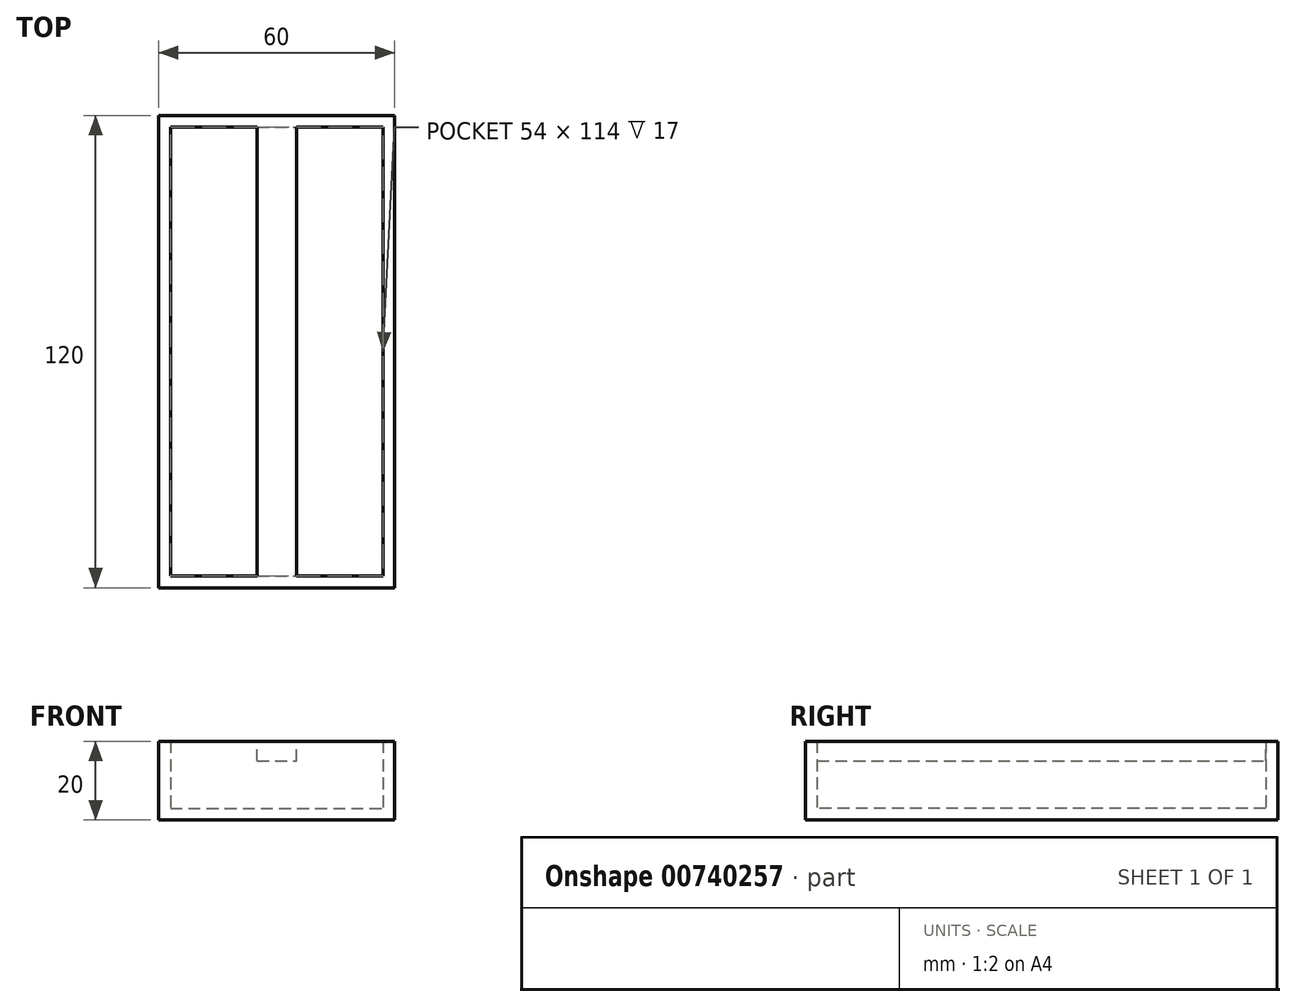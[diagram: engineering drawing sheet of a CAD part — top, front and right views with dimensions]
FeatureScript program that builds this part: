
annotation { "Feature Type Name" : "Feature", "Feature Type Description" : "" }
export const myFeature = defineFeature(function(context is Context, id is Id, definition is map)
    precondition{}
    {
        {
            var Q0;
            Q0=qCreatedBy(makeId("Top.planeOp"),FACE);
            var sketch = newSketch(context, id + "F0", { "sketchPlane" : qUnion([Q0])});
            skLineSegment(sketch, "E0.bottom", {"start": v(-30, 60) * mm, "end": v(30, 60) * mm});
            skLineSegment(sketch, "E0.top", {"start": v(-30, -60) * mm, "end": v(30, -60) * mm});
            skLineSegment(sketch, "E0.left", {"start": v(-30, 60) * mm, "end": v(-30, -60) * mm});
            skLineSegment(sketch, "E0.right", {"start": v(30, 60) * mm, "end": v(30, -60) * mm});
            skPoint(sketch, "E0.middle", {"position": v(0, 0) * mm});
            skSolve(sketch);
        }
        {
            var Q0;
            Q0 = qSketchRegion(id + "F0", true);
            extrude(context, id + "F1", {"entities" : qUnion([Q0]), "depth" : 20 * mm, "offsetDistance" : 25 * mm});
        }
        {
            var Q0;
            Q0=makeQuery(id+"F1.opExtrude","CAP_FACE",FACE,{"disambiguationData":[OSD([sQuery(id+"F0.wireOp",EDGE,"E0.bottom"),sQuery(id+"F0.wireOp",EDGE,"E0.top"),sQuery(id+"F0.wireOp",EDGE,"E0.left"),sQuery(id+"F0.wireOp",EDGE,"E0.right")])],"isStart":false});
            shell(context, id + "F2", {"entities" : qUnion([Q0]), "thickness" : 3 * mm});
        }
        {
            var Q0;
            Q0=qCreatedBy(makeId("Front.planeOp"),FACE);
            var sketch = newSketch(context, id + "F3", { "sketchPlane" : qUnion([Q0])});
            skLineSegment(sketch, "E1.bottom", {"start": v(5, 20) * mm, "end": v(-5, 20) * mm});
            skLineSegment(sketch, "E1.left", {"start": v(5, 20) * mm, "end": v(5, 15) * mm});
            skLineSegment(sketch, "E1.right", {"start": v(-5, 20) * mm, "end": v(-5, 15) * mm});
            skPoint(sketch, "E1.middle", {"position": v(0, 0) * mm});
            skLineSegment(sketch, "E2", {"start": v(5, 15) * mm, "end": v(-5, 15) * mm});
            skPoint(sketch, "E1.top.end.orphan", {"position": v(-5, -20) * mm});
            skPoint(sketch, "E1.top.start.orphan", {"position": v(5, -20) * mm});
            skSolve(sketch);
        }
        {
            var Q0;
            Q0 = qSketchRegion(id + "F3", true);
            extrude(context, id + "F4", {"entities" : qUnion([Q0]), "operationType" : NewBodyOperationType.ADD, "depth" : 60 * mm, "offsetDistance" : 25 * mm});
        }
        {
            var Q0;
            Q0 = qSketchRegion(id + "F3", true);
            extrude(context, id + "F5", {"entities" : qUnion([Q0]), "operationType" : NewBodyOperationType.ADD, "oppositeDirection" : true, "depth" : 60 * mm, "offsetDistance" : 25 * mm});
        }
    });
